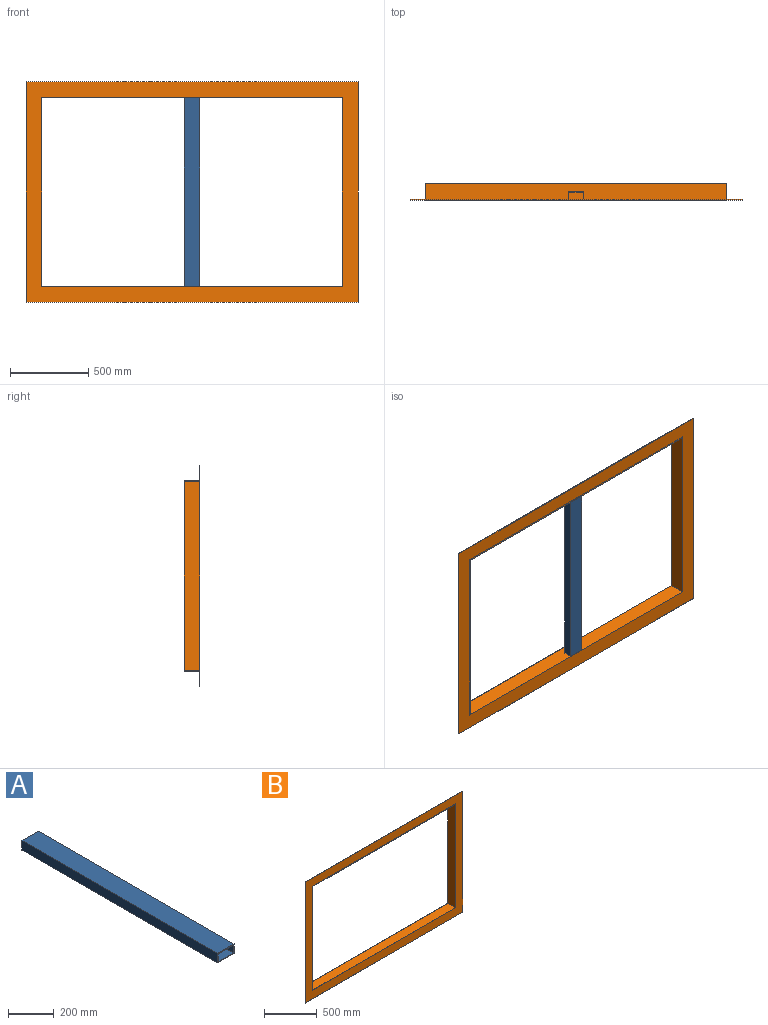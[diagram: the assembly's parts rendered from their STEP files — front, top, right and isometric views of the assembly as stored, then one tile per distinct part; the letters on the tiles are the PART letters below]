
ASSEMBLY  parts=2 mates=1
PART A: 10 faces, bbox 101.6x1204x50.8 mm
  f0: plane 1203.96x101.6mm, normal (0,0,-1), area 122322.3mm2, adj f1,f7,f8,f9
  f1: plane 1203.96x50.8mm, normal (1,0,0), area 61161.2mm2, adj f0,f2,f8,f9
  f2: plane 1203.96x101.6mm, normal (0,0,1), area 122322.3mm2, adj f1,f7,f8,f9
  f3: plane 1203.96x92.46mm, normal (0,0,-1), area 111313.3mm2, adj f4,f6,f8,f9
  f4: plane 1203.96x41.66mm, normal (-1,0,0), area 50152.2mm2, adj f3,f5,f8,f9
  f5: plane 1203.96x92.46mm, normal (0,0,1), area 111313.3mm2, adj f4,f6,f8,f9
  f6: plane 1203.96x41.66mm, normal (1,0,0), area 50152.2mm2, adj f3,f5,f8,f9
  f7: plane 1203.96x50.8mm, normal (-1,0,0), area 61161.2mm2, adj f0,f2,f8,f9
  f8: plane 101.6x50.8mm, normal (0,1,0), area 1309.9mm2, adj f0,f1,f2,f3,f4,f5,f6,f7
  f9: plane 101.6x50.8mm, normal (0,-1,0), area 1309.9mm2, adj f0,f1,f2,f3,f4,f5,f6,f7
PART B: 15 faces, bbox 2119.4x101.6x1408.2 mm
  f0: plane 2119.38x4.57mm, normal (0,0,1), area 9689.8mm2, adj f3,f6,f10,f14
  f1: plane 1916.18x101.6mm, normal (0,0,-1), area 194683.5mm2, adj f4,f7,f10,f12
  f2: plane 1925.32x97.03mm, normal (0,0,1), area 186809.9mm2, adj f5,f8,f12,f14
  f3: plane 1408.18x4.57mm, normal (-1,0,0), area 6438.2mm2, adj f0,f9,f10,f14
  f4: plane 1204.98x101.6mm, normal (1,0,0), area 122425.6mm2, adj f1,f10,f11,f12
  f5: plane 1214.12x97.03mm, normal (-1,0,0), area 117803.6mm2, adj f2,f12,f13,f14
  f6: plane 1408.18x4.57mm, normal (1,0,0), area 6438.2mm2, adj f0,f9,f10,f14
  f7: plane 1204.98x101.6mm, normal (-1,0,0), area 122425.6mm2, adj f1,f10,f11,f12
  f8: plane 1214.12x97.03mm, normal (1,0,0), area 117803.6mm2, adj f2,f12,f13,f14
  f9: plane 2119.38x4.57mm, normal (0,0,-1), area 9689.8mm2, adj f3,f6,f10,f14
  f10: plane 2119.38x1408.18mm, normal (0,-1,0), area 675508.3mm2, adj f0,f1,f3,f4,f6,f7,f9,f11
  f11: plane 1916.18x101.6mm, normal (0,0,1), area 194683.5mm2, adj f4,f7,f10,f12
  f12: plane 1925.32x1214.12mm, normal (0,1,0), area 28623.4mm2, adj f1,f2,f4,f5,f7,f8,f11,f13
  f13: plane 1925.32x97.03mm, normal (0,0,-1), area 186809.9mm2, adj f5,f8,f12,f14
  f14: plane 2119.38x1408.18mm, normal (0,1,0), area 646884.9mm2, adj f0,f2,f3,f5,f6,f8,f9,f13
PLACE A rot(axis=(1,0,0),90deg) t=(0,-27.69,4.57)mm
PLACE B t=(-962.66,-48.51,0)mm
MATE fastened A.f9 <-> B.f11  axis (0,0,-1) through (0,-53.09,4.57)mm
